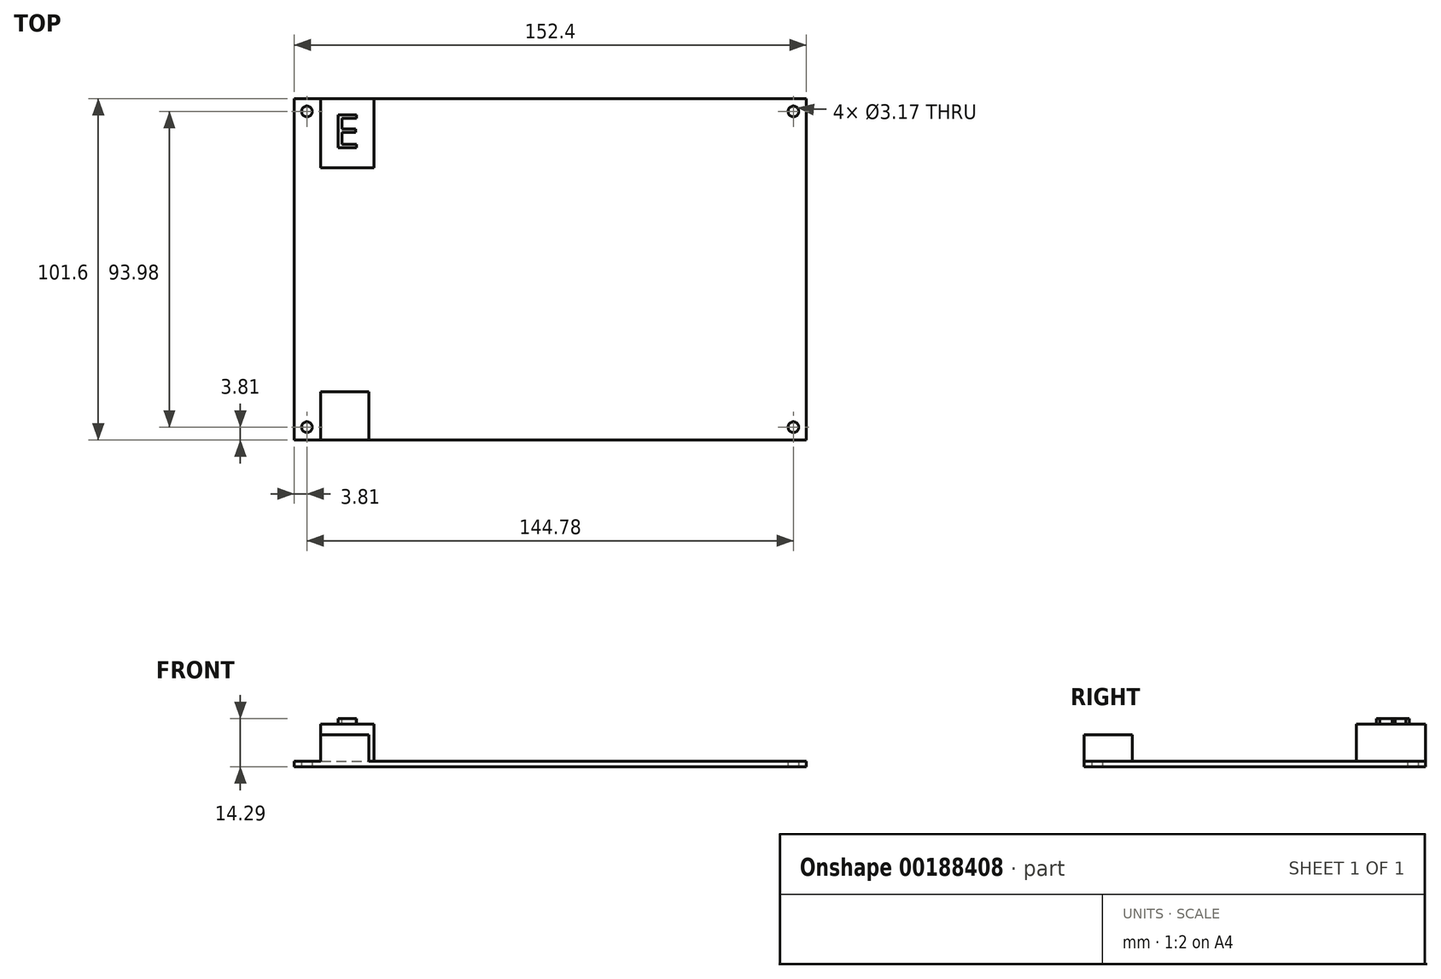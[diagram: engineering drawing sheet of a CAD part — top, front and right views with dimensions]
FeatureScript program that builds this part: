
annotation { "Feature Type Name" : "Feature", "Feature Type Description" : "" }
export const myFeature = defineFeature(function(context is Context, id is Id, definition is map)
    precondition{}
    {
        {
            var Q0;
            Q0=qCreatedBy(makeId("Top.planeOp"),FACE);
            var sketch = newSketch(context, id + "F0", { "sketchPlane" : qUnion([Q0])});
            skLineSegment(sketch, "E0.bottom", {"start": v(0, 0) * mm, "end": v(152.4, 0) * mm});
            skLineSegment(sketch, "E0.top", {"start": v(0, 101.6) * mm, "end": v(152.4, 101.6) * mm});
            skLineSegment(sketch, "E0.left", {"start": v(0, 0) * mm, "end": v(0, 101.6) * mm});
            skLineSegment(sketch, "E0.right", {"start": v(152.4, 0) * mm, "end": v(152.4, 101.6) * mm});
            skLineSegment(sketch, "E1.bottom", {"start": v(76.2, 101.6) * mm, "end": v(76.2, 101.6) * mm});
            skLineSegment(sketch, "E1.top", {"start": v(76.2, 0) * mm, "end": v(76.2, 0) * mm});
            skLineSegment(sketch, "E1.left", {"start": v(76.2, 101.6) * mm, "end": v(76.2, 0) * mm, "construction": true});
            skLineSegment(sketch, "E1.right", {"start": v(76.2, 101.6) * mm, "end": v(76.2, 0) * mm, "construction": true});
            skLineSegment(sketch, "E2.bottom", {"start": v(0, 50.8) * mm, "end": v(152.4, 50.8) * mm, "construction": true});
            skLineSegment(sketch, "E2.top", {"start": v(0, 50.8) * mm, "end": v(152.4, 50.8) * mm, "construction": true});
            skLineSegment(sketch, "E2.left", {"start": v(0, 50.8) * mm, "end": v(0, 50.8) * mm});
            skLineSegment(sketch, "E2.right", {"start": v(152.4, 50.8) * mm, "end": v(152.4, 50.8) * mm});
            skLineSegment(sketch, "E3.0", {"start": v(3.8, 97.8) * mm, "end": v(148.6, 97.8) * mm, "construction": true});
            skLineSegment(sketch, "E3.1", {"start": v(3.8, 3.8) * mm, "end": v(3.8, 97.8) * mm, "construction": true});
            skLineSegment(sketch, "E3.2", {"start": v(3.8, 3.8) * mm, "end": v(148.6, 3.8) * mm, "construction": true});
            skLineSegment(sketch, "E3.3", {"start": v(148.6, 3.8) * mm, "end": v(148.6, 97.8) * mm, "construction": true});
            skCircle(sketch, "E4", {"center": v(3.8, 97.8) * mm, "radius": 1.59 * mm});
            skCircle(sketch, "E5", {"center": v(148.6, 97.8) * mm, "radius": 1.59 * mm});
            skCircle(sketch, "E6", {"center": v(148.6, 3.8) * mm, "radius": 1.59 * mm});
            skCircle(sketch, "E7", {"center": v(3.8, 3.8) * mm, "radius": 1.59 * mm});
            skSolve(sketch);
        }
        {
            var Q0;
            Q0=makeQuery(id+"F0.imprint","IMPRINT",FACE,{"disambiguationData":[TD([[makeQuery(id+"F0.imprint","IMPRINT",EDGE,{"derivedFrom":sQuery(id+"F0.wireOp",EDGE,"E0.bottom")}),1.0]])]});
            extrude(context, id + "F1", {"entities" : qUnion([Q0]), "depth" : 1.59 * mm});
        }
        {
            var Q0;
            Q0=makeQuery(id+"F1.opExtrude","CAP_FACE",FACE,{"disambiguationData":[OSD([sQuery(id+"F0.wireOp",EDGE,"E0.bottom"),sQuery(id+"F0.wireOp",EDGE,"E0.top"),sQuery(id+"F0.wireOp",EDGE,"E0.left"),sQuery(id+"F0.wireOp",EDGE,"E0.right"),sQuery(id+"F0.wireOp",EDGE,"E4"),sQuery(id+"F0.wireOp",EDGE,"E5"),sQuery(id+"F0.wireOp",EDGE,"E6"),sQuery(id+"F0.wireOp",EDGE,"E7")])],"isStart":false});
            var sketch = newSketch(context, id + "F2", { "sketchPlane" : qUnion([Q0])});
            skLineSegment(sketch, "E8.bottom", {"start": v(7.94, 101.6) * mm, "end": v(23.81, 101.6) * mm});
            skLineSegment(sketch, "E8.top", {"start": v(7.94, 80.96) * mm, "end": v(23.81, 80.96) * mm});
            skLineSegment(sketch, "E8.left", {"start": v(7.94, 101.6) * mm, "end": v(7.94, 80.96) * mm});
            skLineSegment(sketch, "E8.right", {"start": v(23.81, 101.6) * mm, "end": v(23.81, 80.96) * mm});
            skSolve(sketch);
        }
        {
            var Q0;
            Q0=makeQuery(id+"F2.imprint","IMPRINT",FACE,{"disambiguationData":[TD([[makeQuery(id+"F2.imprint","IMPRINT",EDGE,{"derivedFrom":sQuery(id+"F2.wireOp",EDGE,"E8.bottom")}),-1.0]])]});
            extrude(context, id + "F3", {"entities" : qUnion([Q0]), "operationType" : NewBodyOperationType.ADD, "depth" : 12.7 * mm});
        }
        {
            var Q0;
            Q0=makeQuery(id+"F1.opExtrude","CAP_FACE",FACE,{"disambiguationData":[OSD([sQuery(id+"F0.wireOp",EDGE,"E0.bottom"),sQuery(id+"F0.wireOp",EDGE,"E0.top"),sQuery(id+"F0.wireOp",EDGE,"E0.left"),sQuery(id+"F0.wireOp",EDGE,"E0.right"),sQuery(id+"F0.wireOp",EDGE,"E4"),sQuery(id+"F0.wireOp",EDGE,"E5"),sQuery(id+"F0.wireOp",EDGE,"E6"),sQuery(id+"F0.wireOp",EDGE,"E7")])],"isStart":false});
            var sketch = newSketch(context, id + "F4", { "sketchPlane" : qUnion([Q0])});
            skLineSegment(sketch, "E9.bottom", {"start": v(7.94, 0) * mm, "end": v(22.23, 0) * mm});
            skLineSegment(sketch, "E9.top", {"start": v(7.94, 14.29) * mm, "end": v(22.22, 14.29) * mm});
            skLineSegment(sketch, "E9.left", {"start": v(7.94, 0) * mm, "end": v(7.94, 14.29) * mm});
            skLineSegment(sketch, "E9.right", {"start": v(22.23, 0) * mm, "end": v(22.22, 14.29) * mm});
            skLineSegment(sketch, "E10.bottom", {"start": v(7.94, 0) * mm, "end": v(0, 0) * mm});
            skLineSegment(sketch, "E10.top", {"start": v(7.94, 0) * mm, "end": v(0, 0) * mm});
            skLineSegment(sketch, "E10.left", {"start": v(7.94, 0) * mm, "end": v(7.94, 0) * mm});
            skLineSegment(sketch, "E10.right", {"start": v(0, 0) * mm, "end": v(0, 0) * mm});
            skSolve(sketch);
        }
        {
            var Q0;
            Q0=makeQuery(id+"F4.imprint","IMPRINT",FACE,{"disambiguationData":[TD([[makeQuery(id+"F4.imprint","IMPRINT",EDGE,{"derivedFrom":sQuery(id+"F4.wireOp",EDGE,"E9.bottom")}),1.0]])]});
            extrude(context, id + "F5", {"entities" : qUnion([Q0]), "operationType" : NewBodyOperationType.ADD, "depth" : 7.94 * mm});
        }
        {
            var Q0;
            Q0=makeQuery(id+"F3.opExtrude","CAP_FACE",FACE,{"disambiguationData":[OSD([sQuery(id+"F2.wireOp",EDGE,"E8.bottom"),sQuery(id+"F2.wireOp",EDGE,"E8.top"),sQuery(id+"F2.wireOp",EDGE,"E8.left"),sQuery(id+"F2.wireOp",EDGE,"E8.right")])],"isStart":false});
            var sketch = newSketch(context, id + "F6", { "sketchPlane" : qUnion([Q0])});
            skText(sketch, "E11", { "text": "E", "fontName": "OpenSans-Regular.ttf"});
            const initialGuessF6  = {"E11": [0.0118, 0.08701, 1, 0, 0.00984]};
            skSetInitialGuess(sketch, initialGuessF6);
            skSolve(sketch);
        }
        {
            var Q0;
            Q0=makeQuery(id+"F6.imprint","IMPRINT",FACE,{"disambiguationData":[TD([[makeQuery(id+"F6.imprint","IMPRINT",EDGE,{"derivedFrom":sQuery(id+"F6.wireOp",EDGE,"E11.sketch_text.stroke-0")}),1.0]])]});
            extrude(context, id + "F7", {"entities" : qUnion([Q0]), "operationType" : NewBodyOperationType.REMOVE, "oppositeDirection" : true, "depth" : 1.59 * mm});
        }
    });
